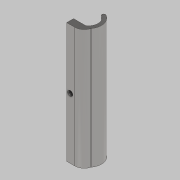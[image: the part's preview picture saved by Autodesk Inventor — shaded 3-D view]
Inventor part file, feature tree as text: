
AUTODESK INVENTOR PART (.ipt)
format: ipt  version: 2021 (Build 250183000, 183)  size: 158,208 bytes
history: native  units: mm
features: extrude x3, fillet x3, sketch x3, sweep x2, projected_geometry x2, other x2, hole x1
ambient origin geometry x8: Origin, YZ Plane, XZ Plane, XY Plane, X Axis, Y Axis, Z Axis, Center Point
bodies: Solid1 (feature_tree)
feature tree (16):
  extrude  "holderProfile"  Depth=3.665191mm
  fillet  "Fillet1"  Radius=2.0mm
  extrude  "holderBase1"  Depth=1.0mm
  fillet  "Fillet2"  Radius=1.0mm
  fillet  "Fillet3"  Radius=70.0mm
  hole  "throughHole"  [1 undecoded]
  sweep  "Sweep1"
  extrude  "Extrusion3"  Depth=1.0mm
  sketch  "Sketch1"  dims[d3=12.042772mm d4=3.665191mm d5=2.0mm]
  sketch  "Sketch2"  dims[d6=5.5mm d7=2.0mm d8=1.0mm d9=70.0mm d10=0.0mm]
  projected_geometry  "Projected Loop1"
  other  "throughholePosition"
  sweep  "sweepLine"
  other  "loopProfile"
  sketch  "Sketch7"  dims[d11=1.0mm d12=10.0mm d13=4.0mm d14=0.0mm d15=1.0mm d16=5.5mm d17=3.0mm d18=6.0mm d19=4.0mm d20=2.0mm d21=90.0deg d22=8.0mm d23=0.0mm d26=4.0mm d27=2.0mm d28=0.0mm d29=0.0mm d30=1.75mm d31=0.0mm d32=5.0mm]
  projected_geometry  "Projected Loop2"
note: 1 required parameter value undecoded (feature->parameter linkage not recoverable at this tier; creation-order binding heuristic only, values carry confidence <= 0.55)
